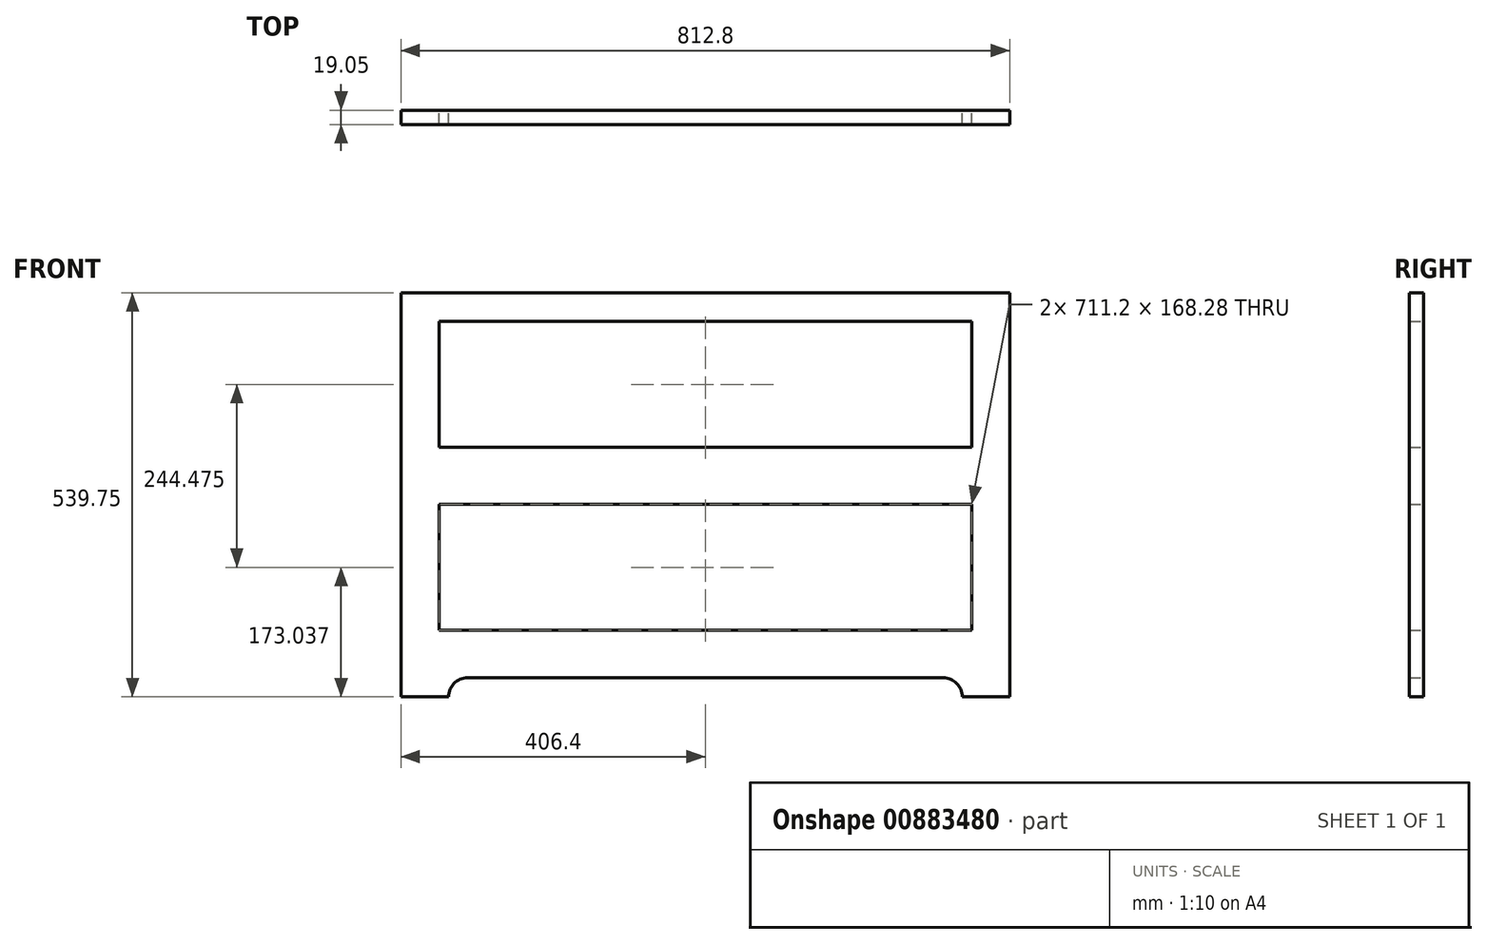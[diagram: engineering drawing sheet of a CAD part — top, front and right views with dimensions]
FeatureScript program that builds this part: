
annotation { "Feature Type Name" : "Feature", "Feature Type Description" : "" }
export const myFeature = defineFeature(function(context is Context, id is Id, definition is map)
    precondition{}
    {
        {
            var Q0;
            Q0=qCreatedBy(makeId("Front.planeOp"),FACE);
            var sketch = newSketch(context, id + "F0", { "sketchPlane" : qUnion([Q0])});
            skLineSegment(sketch, "E0.bottom", {"start": v(0, 0) * mm, "end": v(812.8, 0) * mm});
            skLineSegment(sketch, "E0.top", {"start": v(0, 488.95) * mm, "end": v(812.8, 488.95) * mm});
            skLineSegment(sketch, "E0.left", {"start": v(0, 0) * mm, "end": v(0, 488.95) * mm});
            skLineSegment(sketch, "E0.right", {"start": v(812.8, 0) * mm, "end": v(812.8, 488.95) * mm});
            skLineSegment(sketch, "E1", {"start": v(0, 0) * mm, "end": v(0, -50.8) * mm});
            skLineSegment(sketch, "E2", {"start": v(0, -50.8) * mm, "end": v(63.5, -50.8) * mm});
            skArc(sketch, "E3", {"start": v(88.9, -25.4) * mm, "mid": v(70.94, -32.84) * mm, "end": v(63.5, -50.8) * mm});
            skLineSegment(sketch, "E4", {"start": v(63.5, -50.8) * mm, "end": v(63.5, -146.86) * mm, "construction": true});
            skLineSegment(sketch, "E5", {"start": v(88.9, -25.4) * mm, "end": v(406.4, -25.4) * mm});
            skLineSegment(sketch, "E6", {"start": v(406.4, 488.95) * mm, "end": v(406.4, -170.63) * mm, "construction": true});
            skLineSegment(sketch, "E7.MirrorCS", {"start": v(723.9, -25.4) * mm, "end": v(406.4, -25.4) * mm});
            skArc(sketch, "E8.MirrorCS", {"start": v(723.9, -25.4) * mm, "mid": v(741.86, -32.84) * mm, "end": v(749.3, -50.8) * mm});
            skLineSegment(sketch, "E9.MirrorCS", {"start": v(812.8, -50.8) * mm, "end": v(749.3, -50.8) * mm});
            skLineSegment(sketch, "E10.MirrorCS", {"start": v(812.8, 0) * mm, "end": v(812.8, -50.8) * mm});
            skLineSegment(sketch, "E11", {"start": v(0, 244.48) * mm, "end": v(812.8, 244.48) * mm, "construction": true});
            skLineSegment(sketch, "E12.bottom", {"start": v(50.8, 450.85) * mm, "end": v(762, 450.85) * mm});
            skLineSegment(sketch, "E12.top", {"start": v(50.8, 282.58) * mm, "end": v(762, 282.58) * mm});
            skLineSegment(sketch, "E12.left", {"start": v(50.8, 450.85) * mm, "end": v(50.8, 282.58) * mm});
            skLineSegment(sketch, "E12.right", {"start": v(762, 450.85) * mm, "end": v(762, 282.57) * mm});
            skLineSegment(sketch, "E13.MirrorCS", {"start": v(50.8, 206.38) * mm, "end": v(762, 206.38) * mm});
            skLineSegment(sketch, "E14.MirrorCS", {"start": v(50.8, 38.1) * mm, "end": v(50.8, 206.38) * mm});
            skLineSegment(sketch, "E15.MirrorCS", {"start": v(50.8, 38.1) * mm, "end": v(762, 38.1) * mm});
            skLineSegment(sketch, "E16.MirrorCS", {"start": v(762, 38.1) * mm, "end": v(762, 206.38) * mm});
            skSolve(sketch);
        }
        {
            var Q0;
            Q0=makeQuery(id+"F0.imprint","IMPRINT",FACE,{"disambiguationData":[TD([[makeQuery(id+"F0.imprint","IMPRINT",EDGE,{"derivedFrom":sQuery(id+"F0.wireOp",EDGE,"E0.bottom")}),-1.0]])]});
            var Q1;
            Q1=makeQuery(id+"F0.imprint","IMPRINT",FACE,{"disambiguationData":[TD([[makeQuery(id+"F0.imprint","IMPRINT",EDGE,{"derivedFrom":sQuery(id+"F0.wireOp",EDGE,"E0.bottom")}),1.0]])]});
            extrude(context, id + "F1", {"entities" : qUnion([Q0, Q1]), "depth" : 19.05 * mm, "offsetDistance" : 25.4 * mm});
        }
    });
